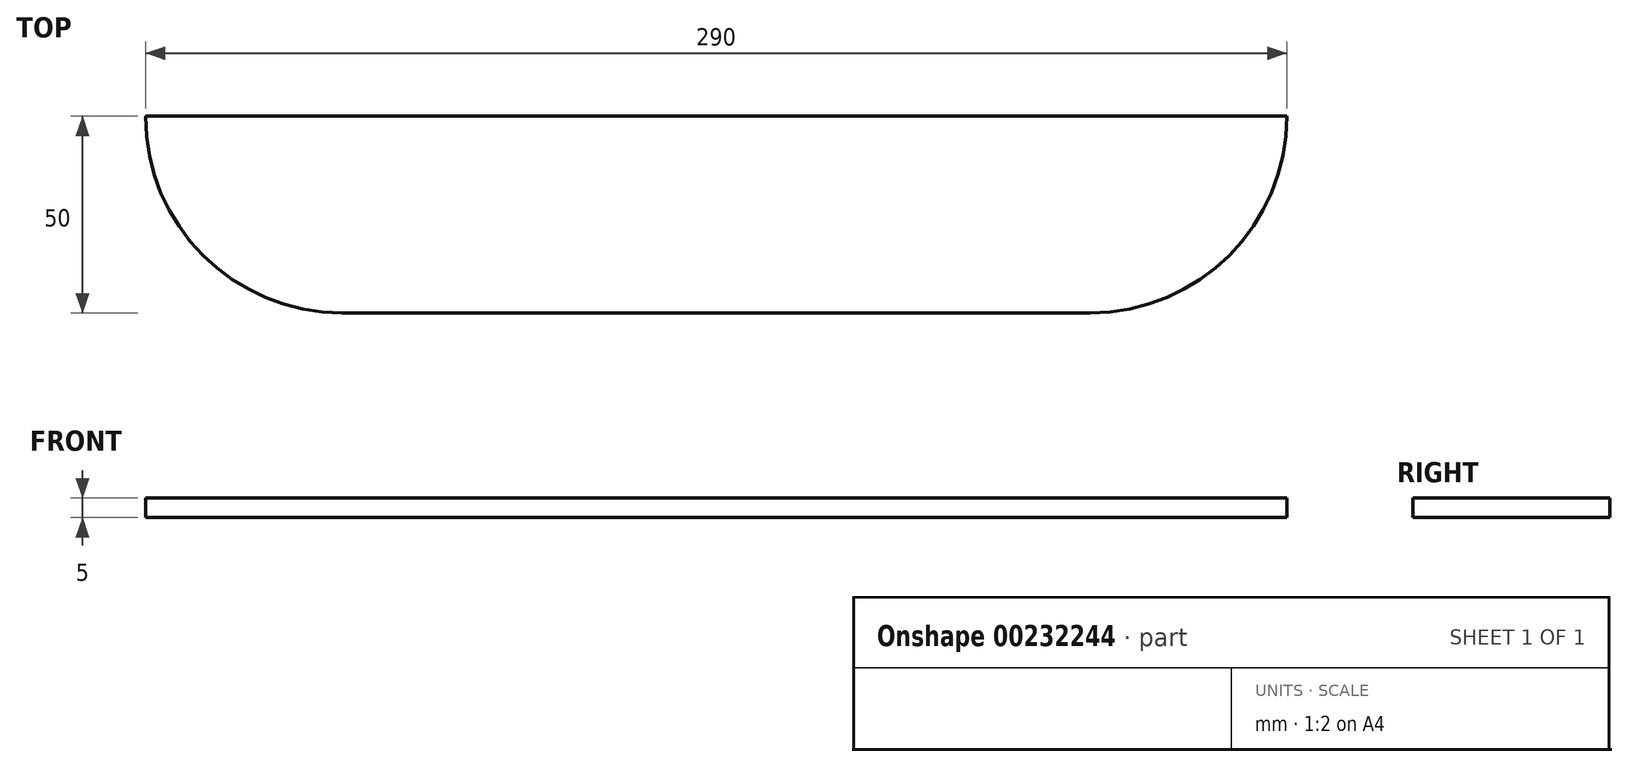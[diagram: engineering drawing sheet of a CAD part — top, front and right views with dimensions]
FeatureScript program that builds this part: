
annotation { "Feature Type Name" : "Feature", "Feature Type Description" : "" }
export const myFeature = defineFeature(function(context is Context, id is Id, definition is map)
    precondition{}
    {
        {
            var Q0;
            Q0=qCreatedBy(makeId("Top.planeOp"),FACE);
            var sketch = newSketch(context, id + "F0", { "sketchPlane" : qUnion([Q0])});
            skLineSegment(sketch, "E0.bottom", {"start": v(-133.43, -46.8) * mm, "end": v(156.57, -46.8) * mm});
            skLineSegment(sketch, "E0.top", {"start": v(-83.43, -96.8) * mm, "end": v(106.57, -96.8) * mm});
            skLineSegment(sketch, "E0.left", {"start": v(-133.43, -46.8) * mm, "end": v(-133.43, -46.8) * mm});
            skLineSegment(sketch, "E0.right", {"start": v(156.57, -46.8) * mm, "end": v(156.57, -46.8) * mm});
            skPoint(sketch, "E1.visualSharp", {"position": v(-133.43, -96.8) * mm});
            skArc(sketch, "E1.filletArc", {"start": v(-133.43, -46.8) * mm, "mid": v(-118.79, -82.15) * mm, "end": v(-83.43, -96.8) * mm});
            skPoint(sketch, "E2.visualSharp", {"position": v(156.57, -96.8) * mm});
            skArc(sketch, "E2.filletArc", {"start": v(106.57, -96.8) * mm, "mid": v(141.92, -82.15) * mm, "end": v(156.57, -46.8) * mm});
            skSolve(sketch);
        }
        {
            var Q0;
            Q0 = qSketchRegion(id + "F0", true);
            extrude(context, id + "F1", {"entities" : qUnion([Q0]), "depth" : 5 * mm});
        }
    });
